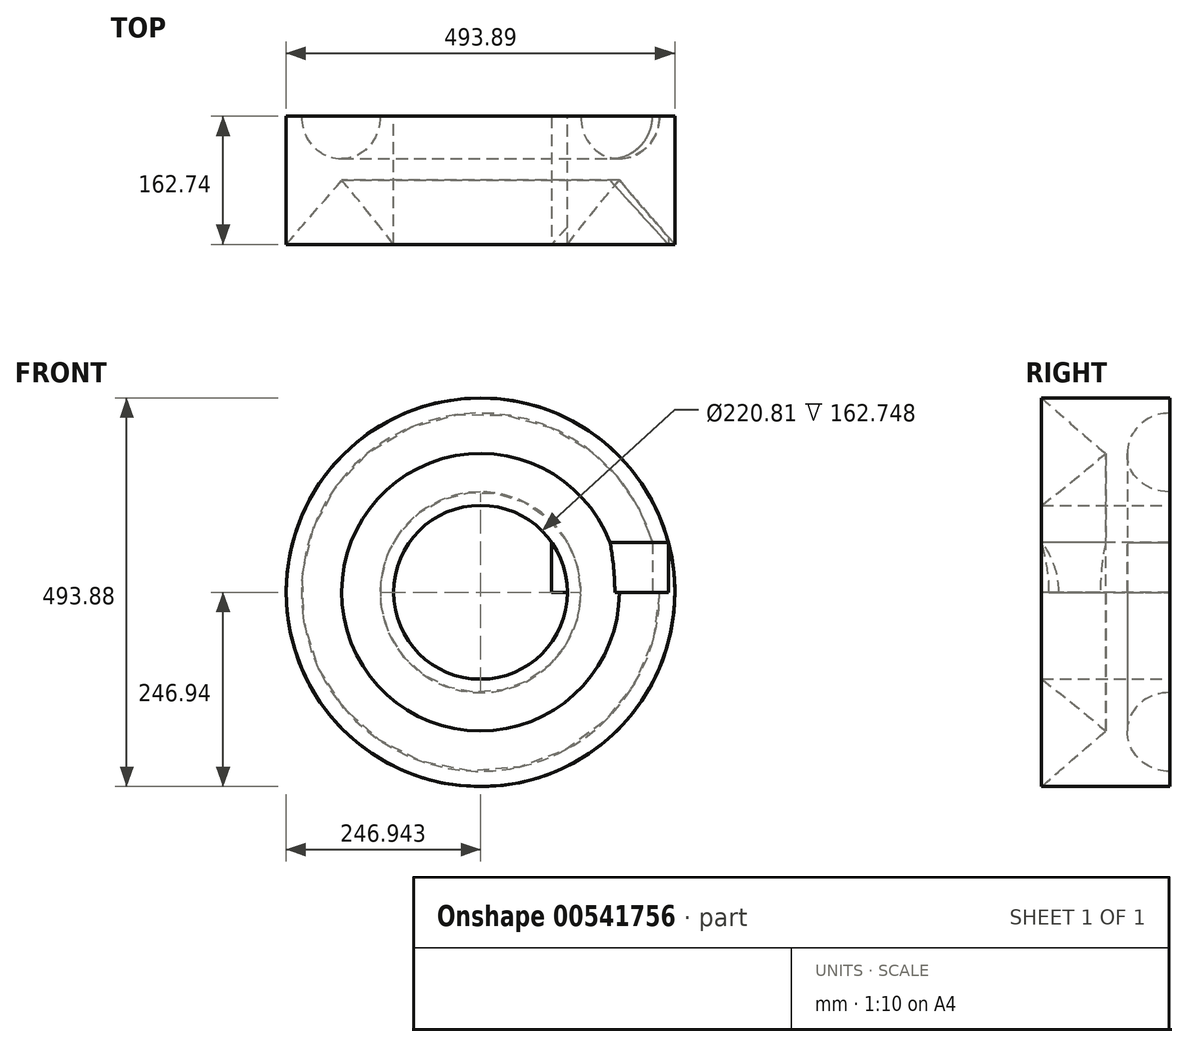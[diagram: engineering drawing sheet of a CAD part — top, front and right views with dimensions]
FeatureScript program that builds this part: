
annotation { "Feature Type Name" : "Feature", "Feature Type Description" : "" }
export const myFeature = defineFeature(function(context is Context, id is Id, definition is map)
    precondition{}
    {
        {
            var Q0;
            Q0=qCreatedBy(makeId("Top.planeOp"),FACE);
            var sketch = newSketch(context, id + "F0", { "sketchPlane" : qUnion([Q0])});
            skLineSegment(sketch, "E0.bottom", {"start": v(74.16, 81.37) * mm, "end": v(53.99, 81.37) * mm});
            skLineSegment(sketch, "E0.left", {"start": v(74.16, 81.37) * mm, "end": v(74.16, -81.37) * mm});
            skLineSegment(sketch, "E0.right", {"start": v(-74.16, 81.37) * mm, "end": v(-74.16, -81.37) * mm});
            skPoint(sketch, "E0.middle", {"position": v(0, 0) * mm});
            skLineSegment(sketch, "E1", {"start": v(0, 0) * mm, "end": v(0, 27.39) * mm});
            skArc(sketch, "E2", {"start": v(-53.99, 81.37) * mm, "mid": v(0, 27.39) * mm, "end": v(53.99, 81.37) * mm});
            skLineSegment(sketch, "E3.trimOffspring", {"start": v(-53.99, 81.37) * mm, "end": v(-74.16, 81.37) * mm});
            skLineSegment(sketch, "E4", {"start": v(0, 0) * mm, "end": v(-74.16, -81.37) * mm});
            skLineSegment(sketch, "E5", {"start": v(0, 0) * mm, "end": v(74.16, -81.37) * mm});
            skSolve(sketch);
        }
        {
            var Q0;
            Q0 = qSketchRegion(id + "F0", true);
            extrude(context, id + "F1", {"entities" : qUnion([Q0]), "depth" : 63.5 * mm, "offsetDistance" : 25.4 * mm});
        }
        {
            var Q0;
            Q0=qCreatedBy(makeId("Top.planeOp"),FACE);
            var sketch = newSketch(context, id + "F2", { "sketchPlane" : qUnion([Q0])});
            skLineSegment(sketch, "E6", {"start": v(-164.48, 167.98) * mm, "end": v(-164.48, -158.02) * mm});
            skSolve(sketch);
        }
        {
            var Q0;
            Q0=makeQuery(id+"F1.opExtrude","CAP_FACE",FACE,{"disambiguationData":[OSD([sQuery(id+"F0.wireOp",EDGE,"E0.bottom"),sQuery(id+"F0.wireOp",EDGE,"E0.left"),sQuery(id+"F0.wireOp",EDGE,"E0.right"),sQuery(id+"F0.wireOp",EDGE,"E2"),sQuery(id+"F0.wireOp",EDGE,"E3.trimOffspring"),sQuery(id+"F0.wireOp",EDGE,"E4"),sQuery(id+"F0.wireOp",EDGE,"E5")])],"isStart":false});
            var Q1;
            Q1=sQuery(id+"F2.wireOp",EDGE,"E6");
            revolve(context, id + "F3", {"operationType" : NewBodyOperationType.ADD, "entities" : qUnion([Q0]), "axis" : qUnion([Q1]), "revolveType" : RevolveType.FULL});
        }
    });
